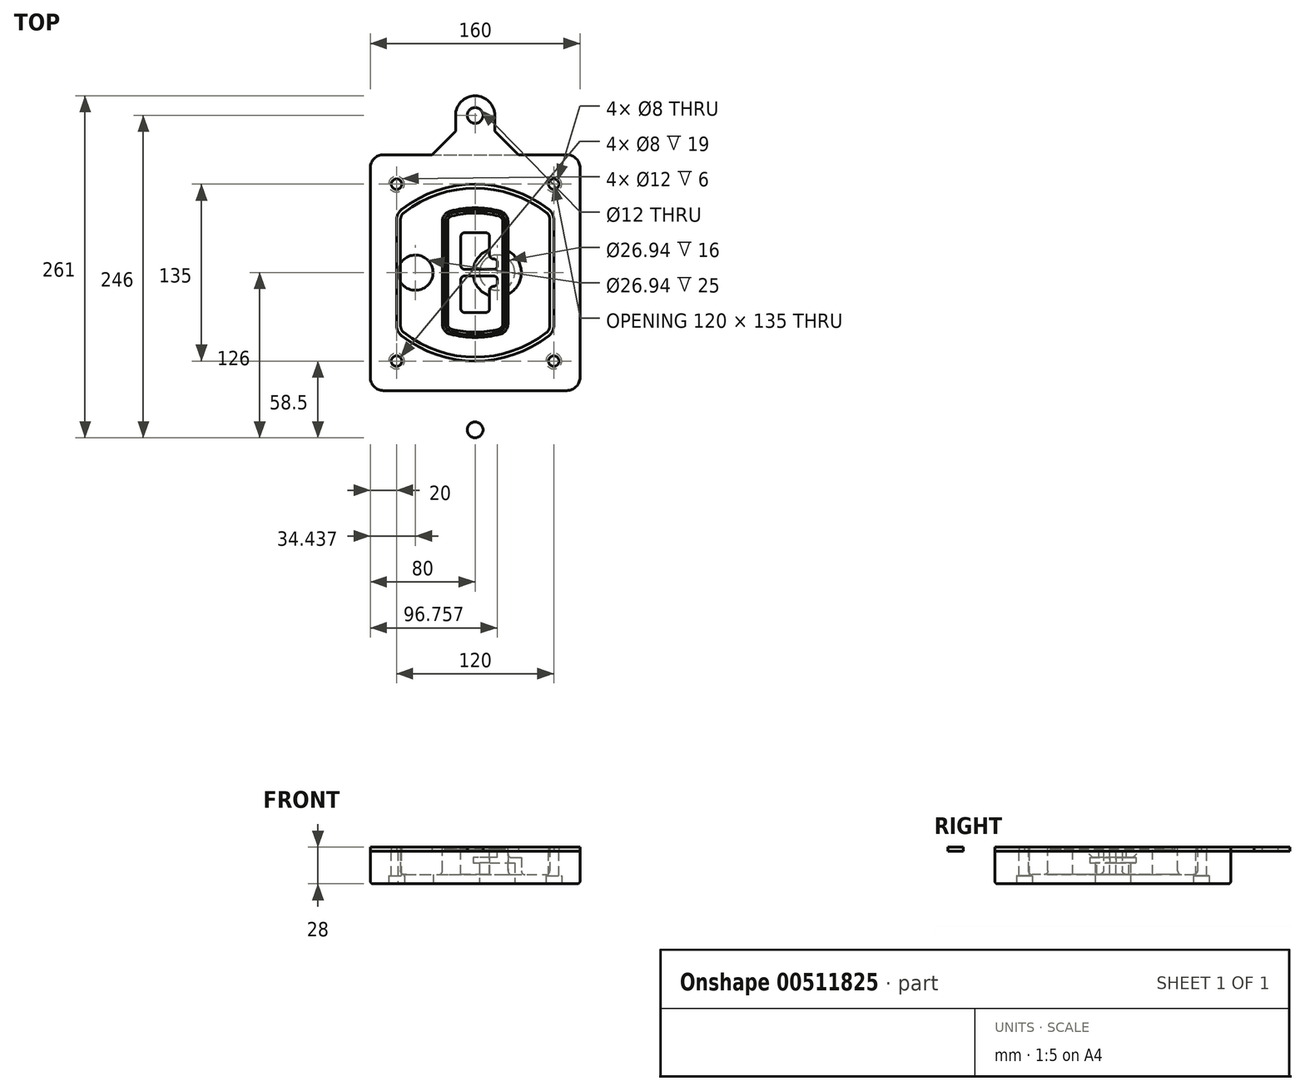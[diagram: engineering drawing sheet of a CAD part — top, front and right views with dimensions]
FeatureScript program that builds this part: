
annotation { "Feature Type Name" : "Feature", "Feature Type Description" : "" }
export const myFeature = defineFeature(function(context is Context, id is Id, definition is map)
    precondition{}
    {
        {
            var Q0;
            Q0=qCreatedBy(makeId("Top.planeOp"),FACE);
            var sketch = newSketch(context, id + "F0", { "sketchPlane" : qUnion([Q0])});
            skPoint(sketch, "E0.rect.middle", {"position": v(0, 0) * mm});
            skLineSegment(sketch, "E1.bottom", {"start": v(-70, -90) * mm, "end": v(70, -90) * mm});
            skLineSegment(sketch, "E1.top", {"start": v(-70, 90) * mm, "end": v(70, 90) * mm});
            skLineSegment(sketch, "E1.left", {"start": v(-80, -80) * mm, "end": v(-80, 80) * mm});
            skLineSegment(sketch, "E1.right", {"start": v(80, -80) * mm, "end": v(80, 80) * mm});
            skLineSegment(sketch, "E2", {"start": v(-80, 90) * mm, "end": v(80, -90) * mm, "construction": true});
            skLineSegment(sketch, "E3", {"start": v(80, 90) * mm, "end": v(-80, -90) * mm, "construction": true});
            skCircle(sketch, "E4", {"center": v(-60, 67.5) * mm, "radius": 4 * mm});
            skCircle(sketch, "E5", {"center": v(60, 67.5) * mm, "radius": 4 * mm});
            skCircle(sketch, "E6", {"center": v(60, -67.5) * mm, "radius": 4 * mm});
            skCircle(sketch, "E7", {"center": v(-60, -67.5) * mm, "radius": 4 * mm});
            skLineSegment(sketch, "E8", {"start": v(-60, 67.5) * mm, "end": v(60, 67.5) * mm, "construction": true});
            skLineSegment(sketch, "E9", {"start": v(60, 67.5) * mm, "end": v(60, -67.5) * mm, "construction": true});
            skLineSegment(sketch, "E10", {"start": v(60, -67.5) * mm, "end": v(-60, -67.5) * mm, "construction": true});
            skLineSegment(sketch, "E11", {"start": v(-60, -67.5) * mm, "end": v(-60, 67.5) * mm, "construction": true});
            skLineSegment(sketch, "E12", {"start": v(-60, 40.3) * mm, "end": v(-60, -40.3) * mm});
            skLineSegment(sketch, "E13", {"start": v(60, 40.3) * mm, "end": v(60, -40.3) * mm});
            skArc(sketch, "E14", {"start": v(56.15, 48.18) * mm, "mid": v(0, 67.5) * mm, "end": v(-56.15, 48.18) * mm});
            skArc(sketch, "E15", {"start": v(-56.15, -48.18) * mm, "mid": v(0, -67.5) * mm, "end": v(56.15, -48.18) * mm});
            skLineSegment(sketch, "E16", {"start": v(-60, 0) * mm, "end": v(60, 0) * mm, "construction": true});
            skPoint(sketch, "E17.visualSharp", {"position": v(-60, -45) * mm});
            skArc(sketch, "E17.filletArc", {"start": v(-60, -40.3) * mm, "mid": v(-58.99, -44.68) * mm, "end": v(-56.15, -48.18) * mm});
            skPoint(sketch, "E18.visualSharp", {"position": v(-60, 45) * mm});
            skArc(sketch, "E18.filletArc", {"start": v(-56.15, 48.18) * mm, "mid": v(-58.99, 44.68) * mm, "end": v(-60, 40.3) * mm});
            skPoint(sketch, "E19.visualSharp", {"position": v(60, 45) * mm});
            skArc(sketch, "E19.filletArc", {"start": v(60, 40.3) * mm, "mid": v(58.99, 44.68) * mm, "end": v(56.15, 48.18) * mm});
            skPoint(sketch, "E20.visualSharp", {"position": v(60, -45) * mm});
            skArc(sketch, "E20.filletArc", {"start": v(56.15, -48.18) * mm, "mid": v(58.99, -44.68) * mm, "end": v(60, -40.3) * mm});
            skPoint(sketch, "E21.visualSharp", {"position": v(-80, 90) * mm});
            skArc(sketch, "E21.filletArc", {"start": v(-70, 90) * mm, "mid": v(-77.07, 87.07) * mm, "end": v(-80, 80) * mm});
            skPoint(sketch, "E22.visualSharp", {"position": v(80, 90) * mm});
            skArc(sketch, "E22.filletArc", {"start": v(80, 80) * mm, "mid": v(77.07, 87.07) * mm, "end": v(70, 90) * mm});
            skPoint(sketch, "E23.visualSharp", {"position": v(80, -90) * mm});
            skArc(sketch, "E23.filletArc", {"start": v(70, -90) * mm, "mid": v(77.07, -87.07) * mm, "end": v(80, -80) * mm});
            skPoint(sketch, "E24.visualSharp", {"position": v(-80, -90) * mm});
            skArc(sketch, "E24.filletArc", {"start": v(-80, -80) * mm, "mid": v(-77.07, -87.07) * mm, "end": v(-70, -90) * mm});
            skArc(sketch, "E25.0", {"start": v(57, 40.3) * mm, "mid": v(56.3, 43.36) * mm, "end": v(54.3, 45.81) * mm});
            skLineSegment(sketch, "E25.1", {"start": v(57, 40.3) * mm, "end": v(57, -40.3) * mm});
            skArc(sketch, "E25.2", {"start": v(54.3, -45.81) * mm, "mid": v(56.3, -43.36) * mm, "end": v(57, -40.3) * mm});
            skArc(sketch, "E25.3", {"start": v(-54.3, -45.81) * mm, "mid": v(0, -64.5) * mm, "end": v(54.3, -45.81) * mm});
            skArc(sketch, "E25.4", {"start": v(-57, -40.3) * mm, "mid": v(-56.3, -43.36) * mm, "end": v(-54.3, -45.81) * mm});
            skArc(sketch, "E25.5", {"start": v(54.3, 45.81) * mm, "mid": v(0, 64.5) * mm, "end": v(-54.3, 45.81) * mm});
            skLineSegment(sketch, "E25.6", {"start": v(-57, 40.3) * mm, "end": v(-57, -40.3) * mm});
            skArc(sketch, "E25.7", {"start": v(-54.3, 45.81) * mm, "mid": v(-56.3, 43.36) * mm, "end": v(-57, 40.3) * mm});
            skArc(sketch, "E26.0", {"start": v(-58.62, 51.33) * mm, "mid": v(-62.58, 46.43) * mm, "end": v(-64, 40.3) * mm});
            skArc(sketch, "E26.1", {"start": v(58.62, 51.33) * mm, "mid": v(0, 71.5) * mm, "end": v(-58.62, 51.33) * mm});
            skArc(sketch, "E26.2", {"start": v(64, 40.3) * mm, "mid": v(62.58, 46.43) * mm, "end": v(58.62, 51.33) * mm});
            skLineSegment(sketch, "E26.3", {"start": v(64, 40.3) * mm, "end": v(64, -40.3) * mm});
            skArc(sketch, "E26.4", {"start": v(58.62, -51.33) * mm, "mid": v(62.58, -46.43) * mm, "end": v(64, -40.3) * mm});
            skLineSegment(sketch, "E26.5", {"start": v(-64, 40.3) * mm, "end": v(-64, -40.3) * mm});
            skArc(sketch, "E26.6", {"start": v(-58.62, -51.33) * mm, "mid": v(0, -71.5) * mm, "end": v(58.62, -51.33) * mm});
            skArc(sketch, "E26.7", {"start": v(-64, -40.3) * mm, "mid": v(-62.58, -46.43) * mm, "end": v(-58.62, -51.33) * mm});
            skSolve(sketch);
        }
        {
            var Q0;
            Q0=makeQuery(id+"F0.imprint","IMPRINT",FACE,{"disambiguationData":[TD([[makeQuery(id+"F0.imprint","IMPRINT",EDGE,{"derivedFrom":sQuery(id+"F0.wireOp",EDGE,"E1.bottom")}),1.0]])]});
            var Q1;
            Q1=makeQuery(id+"F0.imprint","IMPRINT",FACE,{"disambiguationData":[TD([[makeQuery(id+"F0.imprint","IMPRINT",EDGE,{"derivedFrom":sQuery(id+"F0.wireOp",EDGE,"E12")}),1.0]])]});
            var Q2;
            Q2=makeQuery(id+"F0.imprint","IMPRINT",FACE,{"disambiguationData":[TD([[makeQuery(id+"F0.imprint","IMPRINT",EDGE,{"derivedFrom":sQuery(id+"F0.wireOp",EDGE,"E25.0")}),1.0]])]});
            var Q3;
            Q3=makeQuery(id+"F0.imprint","IMPRINT",FACE,{"disambiguationData":[TD([[makeQuery(id+"F0.imprint","IMPRINT",EDGE,{"derivedFrom":sQuery(id+"F0.wireOp",EDGE,"E12")}),-1.0]])]});
            extrude(context, id + "F1", {"entities" : qUnion([Q0, Q1, Q2, Q3]), "oppositeDirection" : true, "depth" : 25 * mm});
        }
        {
            var Q0;
            Q0=makeQuery(id+"F0.imprint","IMPRINT",FACE,{"disambiguationData":[TD([[makeQuery(id+"F0.imprint","IMPRINT",EDGE,{"derivedFrom":sQuery(id+"F0.wireOp",EDGE,"E12")}),1.0]])]});
            extrude(context, id + "F2", {"entities" : qUnion([Q0]), "operationType" : NewBodyOperationType.ADD, "depth" : 3 * mm});
        }
        {
            var Q0;
            Q0=makeQuery(id+"F0.imprint","IMPRINT",FACE,{"disambiguationData":[TD([[makeQuery(id+"F0.imprint","IMPRINT",EDGE,{"derivedFrom":sQuery(id+"F0.wireOp",EDGE,"E25.0")}),1.0]])]});
            extrude(context, id + "F3", {"entities" : qUnion([Q0]), "operationType" : NewBodyOperationType.REMOVE, "oppositeDirection" : true, "depth" : 18 * mm});
        }
        {
            var Q0;
            Q0=makeQuery(id+"F2.opExtrude","CAP_FACE",FACE,{"disambiguationData":[OSD([sQuery(id+"F0.wireOp",EDGE,"E12"),sQuery(id+"F0.wireOp",EDGE,"E13"),sQuery(id+"F0.wireOp",EDGE,"E14"),sQuery(id+"F0.wireOp",EDGE,"E15"),sQuery(id+"F0.wireOp",EDGE,"E17.filletArc"),sQuery(id+"F0.wireOp",EDGE,"E18.filletArc"),sQuery(id+"F0.wireOp",EDGE,"E19.filletArc"),sQuery(id+"F0.wireOp",EDGE,"E20.filletArc"),sQuery(id+"F0.wireOp",EDGE,"E25.0"),sQuery(id+"F0.wireOp",EDGE,"E25.1"),sQuery(id+"F0.wireOp",EDGE,"E25.2"),sQuery(id+"F0.wireOp",EDGE,"E25.3"),sQuery(id+"F0.wireOp",EDGE,"E25.4"),sQuery(id+"F0.wireOp",EDGE,"E25.5"),sQuery(id+"F0.wireOp",EDGE,"E25.6"),sQuery(id+"F0.wireOp",EDGE,"E25.7")])],"isStart":false});
            var sketch = newSketch(context, id + "F4", { "sketchPlane" : qUnion([Q0])});
            skArc(sketch, "E27.0", {"start": v(-19.08, -46.97) * mm, "mid": v(0, -49.5) * mm, "end": v(19.08, -46.97) * mm});
            skArc(sketch, "E28.0", {"start": v(19.08, 46.97) * mm, "mid": v(0, 49.5) * mm, "end": v(-19.08, 46.97) * mm});
            skLineSegment(sketch, "E29", {"start": v(-25, 39.25) * mm, "end": v(-25, -39.25) * mm});
            skLineSegment(sketch, "E30", {"start": v(25, 39.25) * mm, "end": v(25, -39.25) * mm});
            skLineSegment(sketch, "E31", {"start": v(-25, 45.1) * mm, "end": v(25, 45.1) * mm, "construction": true});
            skLineSegment(sketch, "E32", {"start": v(-25, -45.1) * mm, "end": v(25, -45.1) * mm, "construction": true});
            skPoint(sketch, "E33.visualSharp", {"position": v(-25, 45.1) * mm});
            skArc(sketch, "E33.filletArc", {"start": v(-19.08, 46.97) * mm, "mid": v(-23.35, 44.11) * mm, "end": v(-25, 39.25) * mm});
            skPoint(sketch, "E34.visualSharp", {"position": v(25, 45.1) * mm});
            skArc(sketch, "E34.filletArc", {"start": v(25, 39.25) * mm, "mid": v(23.35, 44.11) * mm, "end": v(19.08, 46.97) * mm});
            skPoint(sketch, "E35.visualSharp", {"position": v(25, -45.1) * mm});
            skArc(sketch, "E35.filletArc", {"start": v(19.08, -46.97) * mm, "mid": v(23.35, -44.11) * mm, "end": v(25, -39.25) * mm});
            skPoint(sketch, "E36.visualSharp", {"position": v(-25, -45.1) * mm});
            skArc(sketch, "E36.filletArc", {"start": v(-25, -39.25) * mm, "mid": v(-23.35, -44.11) * mm, "end": v(-19.08, -46.97) * mm});
            skArc(sketch, "E37.0", {"start": v(54.3, 45.81) * mm, "mid": v(0, 64.5) * mm, "end": v(-54.3, 45.81) * mm});
            skArc(sketch, "E37.1", {"start": v(-54.3, 45.81) * mm, "mid": v(-56.3, 43.36) * mm, "end": v(-57, 40.3) * mm});
            skLineSegment(sketch, "E37.2", {"start": v(-57, 40.3) * mm, "end": v(-57, -40.3) * mm});
            skArc(sketch, "E37.3", {"start": v(-57, -40.3) * mm, "mid": v(-56.3, -43.36) * mm, "end": v(-54.3, -45.81) * mm});
            skArc(sketch, "E37.4", {"start": v(-54.3, -45.81) * mm, "mid": v(0, -64.5) * mm, "end": v(54.3, -45.81) * mm});
            skArc(sketch, "E37.5", {"start": v(54.3, -45.81) * mm, "mid": v(56.3, -43.36) * mm, "end": v(57, -40.3) * mm});
            skLineSegment(sketch, "E37.6", {"start": v(57, 40.3) * mm, "end": v(57, -40.3) * mm});
            skArc(sketch, "E37.7", {"start": v(57, 40.3) * mm, "mid": v(56.3, 43.36) * mm, "end": v(54.3, 45.81) * mm});
            skLineSegment(sketch, "E38.0", {"start": v(23, 39.25) * mm, "end": v(23, -39.25) * mm});
            skArc(sketch, "E38.1", {"start": v(18.56, -45.04) * mm, "mid": v(21.76, -42.9) * mm, "end": v(23, -39.25) * mm});
            skArc(sketch, "E38.2", {"start": v(-18.56, -45.04) * mm, "mid": v(0, -47.5) * mm, "end": v(18.56, -45.04) * mm});
            skArc(sketch, "E38.3", {"start": v(-23, -39.25) * mm, "mid": v(-21.76, -42.9) * mm, "end": v(-18.56, -45.04) * mm});
            skLineSegment(sketch, "E38.4", {"start": v(-23, 39.25) * mm, "end": v(-23, -39.25) * mm});
            skArc(sketch, "E38.5", {"start": v(23, 39.25) * mm, "mid": v(21.76, 42.9) * mm, "end": v(18.56, 45.04) * mm});
            skArc(sketch, "E38.6", {"start": v(-18.56, 45.04) * mm, "mid": v(-21.76, 42.9) * mm, "end": v(-23, 39.25) * mm});
            skArc(sketch, "E38.7", {"start": v(18.56, 45.04) * mm, "mid": v(0, 47.5) * mm, "end": v(-18.56, 45.04) * mm});
            skArc(sketch, "E39.0", {"start": v(21, 39.25) * mm, "mid": v(20.18, 41.68) * mm, "end": v(18.04, 43.1) * mm});
            skLineSegment(sketch, "E39.1", {"start": v(21, 39.25) * mm, "end": v(21, -39.25) * mm});
            skArc(sketch, "E39.2", {"start": v(18.04, -43.1) * mm, "mid": v(20.18, -41.68) * mm, "end": v(21, -39.25) * mm});
            skArc(sketch, "E39.3", {"start": v(-18.04, -43.1) * mm, "mid": v(0, -45.5) * mm, "end": v(18.04, -43.1) * mm});
            skArc(sketch, "E39.4", {"start": v(-21, -39.25) * mm, "mid": v(-20.18, -41.68) * mm, "end": v(-18.04, -43.1) * mm});
            skArc(sketch, "E39.5", {"start": v(18.04, 43.1) * mm, "mid": v(0, 45.5) * mm, "end": v(-18.04, 43.1) * mm});
            skLineSegment(sketch, "E39.6", {"start": v(-21, 39.25) * mm, "end": v(-21, -39.25) * mm});
            skArc(sketch, "E39.7", {"start": v(-18.04, 43.1) * mm, "mid": v(-20.18, 41.68) * mm, "end": v(-21, 39.25) * mm});
            skLineSegment(sketch, "E40", {"start": v(-25, 0) * mm, "end": v(25, 0) * mm, "construction": true});
            skLineSegment(sketch, "E41", {"start": v(-11, 5.5) * mm, "end": v(-11, 27.5) * mm});
            skLineSegment(sketch, "E42", {"start": v(-8, 30.5) * mm, "end": v(8, 30.5) * mm});
            skLineSegment(sketch, "E43", {"start": v(11, 27.5) * mm, "end": v(11, 13.5) * mm});
            skLineSegment(sketch, "E44", {"start": v(14, 10.5) * mm, "end": v(14, 10.5) * mm});
            skLineSegment(sketch, "E45", {"start": v(17, 7.5) * mm, "end": v(17, 5.5) * mm});
            skLineSegment(sketch, "E46", {"start": v(14, 2.5) * mm, "end": v(-8, 2.5) * mm});
            skPoint(sketch, "E47.visualSharp", {"position": v(-11, 30.5) * mm});
            skArc(sketch, "E47.filletArc", {"start": v(-8, 30.5) * mm, "mid": v(-10.12, 29.62) * mm, "end": v(-11, 27.5) * mm});
            skPoint(sketch, "E48.visualSharp", {"position": v(11, 30.5) * mm});
            skArc(sketch, "E48.filletArc", {"start": v(11, 27.5) * mm, "mid": v(10.12, 29.62) * mm, "end": v(8, 30.5) * mm});
            skPoint(sketch, "E49.visualSharp", {"position": v(11, 10.5) * mm});
            skArc(sketch, "E49.filletArc", {"start": v(11, 13.5) * mm, "mid": v(11.88, 11.38) * mm, "end": v(14, 10.5) * mm});
            skPoint(sketch, "E50.visualSharp", {"position": v(17, 10.5) * mm});
            skArc(sketch, "E50.filletArc", {"start": v(17, 7.5) * mm, "mid": v(16.12, 9.62) * mm, "end": v(14, 10.5) * mm});
            skPoint(sketch, "E51.visualSharp", {"position": v(17, 2.5) * mm});
            skArc(sketch, "E51.filletArc", {"start": v(14, 2.5) * mm, "mid": v(16.12, 3.38) * mm, "end": v(17, 5.5) * mm});
            skPoint(sketch, "E52.visualSharp", {"position": v(-11, 2.5) * mm});
            skArc(sketch, "E52.filletArc", {"start": v(-11, 5.5) * mm, "mid": v(-10.12, 3.38) * mm, "end": v(-8, 2.5) * mm});
            skLineSegment(sketch, "E53.0.MirrorCS", {"start": v(14, -2.5) * mm, "end": v(-8, -2.5) * mm});
            skArc(sketch, "E54.0.MirrorCS", {"start": v(-11, -5.5) * mm, "mid": v(-10.12, -3.38) * mm, "end": v(-8, -2.5) * mm});
            skLineSegment(sketch, "E55.0.MirrorCS", {"start": v(-11, -5.5) * mm, "end": v(-11, -27.5) * mm});
            skArc(sketch, "E56.0.MirrorCS", {"start": v(-8, -30.5) * mm, "mid": v(-10.12, -29.62) * mm, "end": v(-11, -27.5) * mm});
            skLineSegment(sketch, "E57.0.MirrorCS", {"start": v(-8, -30.5) * mm, "end": v(8, -30.5) * mm});
            skArc(sketch, "E58.0.MirrorCS", {"start": v(11, -27.5) * mm, "mid": v(10.12, -29.62) * mm, "end": v(8, -30.5) * mm});
            skLineSegment(sketch, "E59.0.MirrorCS", {"start": v(11, -27.5) * mm, "end": v(11, -13.5) * mm});
            skArc(sketch, "E60.0.MirrorCS", {"start": v(11, -13.5) * mm, "mid": v(11.88, -11.38) * mm, "end": v(14, -10.5) * mm});
            skArc(sketch, "E61.0.MirrorCS", {"start": v(17, -7.5) * mm, "mid": v(16.12, -9.62) * mm, "end": v(14, -10.5) * mm});
            skLineSegment(sketch, "E62.0.MirrorCS", {"start": v(17, -7.5) * mm, "end": v(17, -5.5) * mm});
            skArc(sketch, "E63.0.MirrorCS", {"start": v(14, -2.5) * mm, "mid": v(16.12, -3.38) * mm, "end": v(17, -5.5) * mm});
            skSolve(sketch);
        }
        {
            var Q0;
            Q0=makeQuery(id+"F4.imprint","IMPRINT",FACE,{"disambiguationData":[TD([[makeQuery(id+"F4.imprint","IMPRINT",EDGE,{"derivedFrom":sQuery(id+"F4.wireOp",EDGE,"E27.0")}),1.0]])]});
            var Q1;
            Q1=makeQuery(id+"F4.imprint","IMPRINT",FACE,{"disambiguationData":[TD([[makeQuery(id+"F4.imprint","IMPRINT",EDGE,{"derivedFrom":sQuery(id+"F4.wireOp",EDGE,"E38.0")}),-1.0]])]});
            var Q2;
            Q2=makeQuery(id+"F4.imprint","IMPRINT",FACE,{"disambiguationData":[TD([[makeQuery(id+"F4.imprint","IMPRINT",EDGE,{"derivedFrom":sQuery(id+"F4.wireOp",EDGE,"E39.0")}),1.0]])]});
            extrude(context, id + "F5", {"entities" : qUnion([Q0, Q1, Q2]), "operationType" : NewBodyOperationType.ADD, "endBound" : BoundingType.UP_TO_NEXT, "oppositeDirection" : true, "depth" : 25 * mm});
        }
        {
            var Q0;
            Q0=makeQuery(id+"F4.imprint","IMPRINT",FACE,{"disambiguationData":[TD([[makeQuery(id+"F4.imprint","IMPRINT",EDGE,{"derivedFrom":sQuery(id+"F4.wireOp",EDGE,"E38.0")}),-1.0]])]});
            extrude(context, id + "F6", {"entities" : qUnion([Q0]), "operationType" : NewBodyOperationType.REMOVE, "oppositeDirection" : true, "depth" : 2 * mm});
        }
        {
            var Q0;
            Q0=makeQuery(id+"F1.opExtrude","CAP_FACE",FACE,{"disambiguationData":[OSD([sQuery(id+"F0.wireOp",EDGE,"E1.bottom"),sQuery(id+"F0.wireOp",EDGE,"E1.top"),sQuery(id+"F0.wireOp",EDGE,"E1.left"),sQuery(id+"F0.wireOp",EDGE,"E1.right"),sQuery(id+"F0.wireOp",EDGE,"E4"),sQuery(id+"F0.wireOp",EDGE,"E5"),sQuery(id+"F0.wireOp",EDGE,"E6"),sQuery(id+"F0.wireOp",EDGE,"E7"),sQuery(id+"F0.wireOp",EDGE,"E21.filletArc"),sQuery(id+"F0.wireOp",EDGE,"E22.filletArc"),sQuery(id+"F0.wireOp",EDGE,"E23.filletArc"),sQuery(id+"F0.wireOp",EDGE,"E24.filletArc")])],"isStart":false});
            var sketch = newSketch(context, id + "F7", { "sketchPlane" : qUnion([Q0])});
            skCircle(sketch, "E64", {"center": v(16.76, 0) * mm, "radius": 13.47 * mm});
            skCircle(sketch, "E65", {"center": v(-45.56, 0) * mm, "radius": 13.47 * mm});
            skLineSegment(sketch, "E66", {"start": v(80, 0) * mm, "end": v(-80, 0) * mm});
            skCircle(sketch, "E67", {"center": v(16.76, 0) * mm, "radius": 18.47 * mm});
            skCircle(sketch, "E68", {"center": v(60, -67.5) * mm, "radius": 6 * mm});
            skCircle(sketch, "E69", {"center": v(-60, -67.5) * mm, "radius": 6 * mm});
            skCircle(sketch, "E70", {"center": v(-60, 67.5) * mm, "radius": 6 * mm});
            skCircle(sketch, "E71", {"center": v(60, 67.5) * mm, "radius": 6 * mm});
            skSolve(sketch);
        }
        {
            var Q0;
            {var subQ1=sQuery(id+"F7.wireOp",EDGE,"E66");var subQ4=sQuery(id+"F7.wireOp",EDGE,"E64");var subQ6=makeQuery(id+"F7.imprint","INTERSECT",VERTEX,{"disambiguationData":[OD(0.0)],"derivedFrom":[subQ4,subQ1]});Q0=makeQuery(id+"F7.imprint","IMPRINT",FACE,{"disambiguationData":[TD([[makeQuery(id+"F7.imprint","IMPRINT",EDGE,{"disambiguationData":[TD([[subQ6,-1.0]])],"derivedFrom":subQ4}),-1.0]])]});}
            var Q1;
            {var subQ0=sQuery(id+"F7.wireOp",EDGE,"E66");var subQ1=sQuery(id+"F7.wireOp",EDGE,"E64");var subQ3=makeQuery(id+"F7.imprint","INTERSECT",VERTEX,{"disambiguationData":[OD(0.0)],"derivedFrom":[subQ1,subQ0]});Q1=makeQuery(id+"F7.imprint","IMPRINT",FACE,{"disambiguationData":[TD([[makeQuery(id+"F7.imprint","IMPRINT",EDGE,{"disambiguationData":[TD([[subQ3,-1.0]])],"derivedFrom":subQ1}),1.0]])]});}
            var Q2;
            {var subQ0=sQuery(id+"F7.wireOp",EDGE,"E66");var subQ1=sQuery(id+"F7.wireOp",EDGE,"E64");var subQ3=makeQuery(id+"F7.imprint","INTERSECT",VERTEX,{"disambiguationData":[OD(0.0)],"derivedFrom":[subQ1,subQ0]});Q2=makeQuery(id+"F7.imprint","IMPRINT",FACE,{"disambiguationData":[TD([[makeQuery(id+"F7.imprint","IMPRINT",EDGE,{"disambiguationData":[TD([[subQ3,1.0]])],"derivedFrom":subQ1}),1.0]])]});}
            var Q3;
            {var subQ1=sQuery(id+"F7.wireOp",EDGE,"E66");var subQ4=sQuery(id+"F7.wireOp",EDGE,"E64");var subQ6=makeQuery(id+"F7.imprint","INTERSECT",VERTEX,{"disambiguationData":[OD(0.0)],"derivedFrom":[subQ4,subQ1]});Q3=makeQuery(id+"F7.imprint","IMPRINT",FACE,{"disambiguationData":[TD([[makeQuery(id+"F7.imprint","IMPRINT",EDGE,{"disambiguationData":[TD([[subQ6,1.0]])],"derivedFrom":subQ4}),-1.0]])]});}
            extrude(context, id + "F8", {"entities" : qUnion([Q0, Q1, Q2, Q3]), "operationType" : NewBodyOperationType.ADD, "oppositeDirection" : true, "depth" : 20 * mm});
        }
        {
            var Q0;
            {var subQ0=sQuery(id+"F7.wireOp",EDGE,"E66");var subQ1=sQuery(id+"F7.wireOp",EDGE,"E64");var subQ3=makeQuery(id+"F7.imprint","INTERSECT",VERTEX,{"disambiguationData":[OD(0.0)],"derivedFrom":[subQ1,subQ0]});Q0=makeQuery(id+"F7.imprint","IMPRINT",FACE,{"disambiguationData":[TD([[makeQuery(id+"F7.imprint","IMPRINT",EDGE,{"disambiguationData":[TD([[subQ3,-1.0]])],"derivedFrom":subQ1}),1.0]])]});}
            var Q1;
            {var subQ0=sQuery(id+"F7.wireOp",EDGE,"E66");var subQ1=sQuery(id+"F7.wireOp",EDGE,"E64");var subQ3=makeQuery(id+"F7.imprint","INTERSECT",VERTEX,{"disambiguationData":[OD(0.0)],"derivedFrom":[subQ1,subQ0]});Q1=makeQuery(id+"F7.imprint","IMPRINT",FACE,{"disambiguationData":[TD([[makeQuery(id+"F7.imprint","IMPRINT",EDGE,{"disambiguationData":[TD([[subQ3,1.0]])],"derivedFrom":subQ1}),1.0]])]});}
            extrude(context, id + "F9", {"entities" : qUnion([Q0, Q1]), "operationType" : NewBodyOperationType.REMOVE, "oppositeDirection" : true, "depth" : 16 * mm});
        }
        {
            var Q0;
            {var subQ0=sQuery(id+"F7.wireOp",EDGE,"E66");var subQ1=sQuery(id+"F7.wireOp",EDGE,"E65");var subQ3=makeQuery(id+"F7.imprint","INTERSECT",VERTEX,{"disambiguationData":[OD(0.0)],"derivedFrom":[subQ1,subQ0]});Q0=makeQuery(id+"F7.imprint","IMPRINT",FACE,{"disambiguationData":[TD([[makeQuery(id+"F7.imprint","IMPRINT",EDGE,{"disambiguationData":[TD([[subQ3,-1.0]])],"derivedFrom":subQ1}),1.0]])]});}
            var Q1;
            {var subQ0=sQuery(id+"F7.wireOp",EDGE,"E66");var subQ1=sQuery(id+"F7.wireOp",EDGE,"E65");var subQ3=makeQuery(id+"F7.imprint","INTERSECT",VERTEX,{"disambiguationData":[OD(0.0)],"derivedFrom":[subQ1,subQ0]});Q1=makeQuery(id+"F7.imprint","IMPRINT",FACE,{"disambiguationData":[TD([[makeQuery(id+"F7.imprint","IMPRINT",EDGE,{"disambiguationData":[TD([[subQ3,1.0]])],"derivedFrom":subQ1}),1.0]])]});}
            extrude(context, id + "F10", {"entities" : qUnion([Q0, Q1]), "operationType" : NewBodyOperationType.REMOVE, "oppositeDirection" : true, "depth" : 25 * mm});
        }
        {
            var Q0;
            Q0=makeQuery(id+"F7.imprint","IMPRINT",FACE,{"disambiguationData":[TD([[makeQuery(id+"F7.imprint","IMPRINT",EDGE,{"derivedFrom":sQuery(id+"F7.wireOp",EDGE,"E68")}),1.0]])]});
            var Q1;
            Q1=makeQuery(id+"F7.imprint","IMPRINT",FACE,{"disambiguationData":[TD([[makeQuery(id+"F7.imprint","IMPRINT",EDGE,{"derivedFrom":makeQuery(id+"F1.opExtrude","CAP_EDGE",EDGE,{"disambiguationData":[OSD([sQuery(id+"F0.wireOp",EDGE,"E5")])],"isStart":false})}),-1.0]])]});
            var Q2;
            Q2=makeQuery(id+"F7.imprint","IMPRINT",FACE,{"disambiguationData":[TD([[makeQuery(id+"F7.imprint","IMPRINT",EDGE,{"derivedFrom":sQuery(id+"F7.wireOp",EDGE,"E69")}),1.0]])]});
            var Q3;
            Q3=makeQuery(id+"F7.imprint","IMPRINT",FACE,{"disambiguationData":[TD([[makeQuery(id+"F7.imprint","IMPRINT",EDGE,{"derivedFrom":makeQuery(id+"F1.opExtrude","CAP_EDGE",EDGE,{"disambiguationData":[OSD([sQuery(id+"F0.wireOp",EDGE,"E4")])],"isStart":false})}),-1.0]])]});
            var Q4;
            Q4=makeQuery(id+"F7.imprint","IMPRINT",FACE,{"disambiguationData":[TD([[makeQuery(id+"F7.imprint","IMPRINT",EDGE,{"derivedFrom":sQuery(id+"F7.wireOp",EDGE,"E70")}),1.0]])]});
            var Q5;
            Q5=makeQuery(id+"F7.imprint","IMPRINT",FACE,{"disambiguationData":[TD([[makeQuery(id+"F7.imprint","IMPRINT",EDGE,{"derivedFrom":makeQuery(id+"F1.opExtrude","CAP_EDGE",EDGE,{"disambiguationData":[OSD([sQuery(id+"F0.wireOp",EDGE,"E7")])],"isStart":false})}),-1.0]])]});
            var Q6;
            Q6=makeQuery(id+"F7.imprint","IMPRINT",FACE,{"disambiguationData":[TD([[makeQuery(id+"F7.imprint","IMPRINT",EDGE,{"derivedFrom":sQuery(id+"F7.wireOp",EDGE,"E71")}),1.0]])]});
            var Q7;
            Q7=makeQuery(id+"F7.imprint","IMPRINT",FACE,{"disambiguationData":[TD([[makeQuery(id+"F7.imprint","IMPRINT",EDGE,{"derivedFrom":makeQuery(id+"F1.opExtrude","CAP_EDGE",EDGE,{"disambiguationData":[OSD([sQuery(id+"F0.wireOp",EDGE,"E6")])],"isStart":false})}),-1.0]])]});
            extrude(context, id + "F11", {"entities" : qUnion([Q0, Q1, Q2, Q3, Q4, Q5, Q6, Q7]), "operationType" : NewBodyOperationType.REMOVE, "oppositeDirection" : true, "depth" : 6 * mm});
        }
        {
            var Q0;
            Q0=makeQuery(id+"F9.boolean.opBoolean","COPY",FACE,{"derivedFrom":makeQuery(id+"F9.opExtrude","CAP_FACE",FACE,{"disambiguationData":[OSD([sQuery(id+"F7.wireOp",EDGE,"E64")])],"isStart":false})});
            var sketch = newSketch(context, id + "F12", { "sketchPlane" : qUnion([Q0])});
            skArc(sketch, "E72.0", {"start": v(11, 17.55) * mm, "mid": v(2.57, 11.82) * mm, "end": v(-1.54, 2.5) * mm});
            skArc(sketch, "E72.1", {"start": v(-1.54, -2.5) * mm, "mid": v(2.57, -11.82) * mm, "end": v(11, -17.55) * mm});
            skLineSegment(sketch, "E73", {"start": v(-1.54, -2.5) * mm, "end": v(14, -2.5) * mm});
            skLineSegment(sketch, "E74.0", {"start": v(14, 2.5) * mm, "end": v(-1.54, 2.5) * mm});
            skArc(sketch, "E74.1", {"start": v(14, 2.5) * mm, "mid": v(16.12, 3.38) * mm, "end": v(17, 5.5) * mm});
            skLineSegment(sketch, "E74.2", {"start": v(17, 7.5) * mm, "end": v(17, 5.5) * mm});
            skArc(sketch, "E74.3", {"start": v(17, 7.5) * mm, "mid": v(16.12, 9.62) * mm, "end": v(14, 10.5) * mm});
            skArc(sketch, "E74.4", {"start": v(11, 13.5) * mm, "mid": v(11.88, 11.38) * mm, "end": v(14, 10.5) * mm});
            skLineSegment(sketch, "E74.5", {"start": v(11, 17.55) * mm, "end": v(11, 13.5) * mm});
            skLineSegment(sketch, "E74.7", {"start": v(14, -2.5) * mm, "end": v(-1.54, -2.5) * mm});
            skArc(sketch, "E74.8", {"start": v(14, -2.5) * mm, "mid": v(16.12, -3.38) * mm, "end": v(17, -5.5) * mm});
            skLineSegment(sketch, "E74.9", {"start": v(17, -7.5) * mm, "end": v(17, -5.5) * mm});
            skArc(sketch, "E74.10", {"start": v(17, -7.5) * mm, "mid": v(16.12, -9.62) * mm, "end": v(14, -10.5) * mm});
            skArc(sketch, "E74.11", {"start": v(11, -13.5) * mm, "mid": v(11.88, -11.38) * mm, "end": v(14, -10.5) * mm});
            skLineSegment(sketch, "E74.12", {"start": v(11, -17.55) * mm, "end": v(11, -13.5) * mm});
            skPoint(sketch, "E75.orphan", {"position": v(11, -27.5) * mm});
            skPoint(sketch, "E76.orphan", {"position": v(-8, -2.5) * mm});
            skPoint(sketch, "E77.orphan", {"position": v(-8, 2.5) * mm});
            skPoint(sketch, "E78.orphan", {"position": v(11, 27.5) * mm});
            skSolve(sketch);
        }
        {
            var Q0;
            {var subQ7=sQuery(id+"F12.wireOp",EDGE,"E72.0");var subQ14=sQuery(id+"F12.wireOp",EDGE,"E72.1");var subQ16=sQuery(id+"F12.wireOp",EDGE,"E74.1");var subQ18=sQuery(id+"F12.wireOp",EDGE,"E74.8");Q0=qUnion([makeQuery(id+"F12.imprint","IMPRINT",FACE,{"disambiguationData":[TD([[makeQuery(id+"F12.imprint","IMPRINT",EDGE,{"derivedFrom":subQ7}),1.0]])]}),makeQuery(id+"F12.imprint","IMPRINT",FACE,{"disambiguationData":[TD([[makeQuery(id+"F12.imprint","IMPRINT",EDGE,{"derivedFrom":subQ14}),1.0]])]}),makeQuery(id+"F12.imprint","IMPRINT",FACE,{"disambiguationData":[TD([[makeQuery(id+"F12.imprint","IMPRINT",EDGE,{"derivedFrom":subQ16}),1.0]])]}),makeQuery(id+"F12.imprint","IMPRINT",FACE,{"disambiguationData":[TD([[makeQuery(id+"F12.imprint","IMPRINT",EDGE,{"derivedFrom":subQ18}),-1.0]])]})]);}
            var Q1;
            Q1=makeQuery(id+"F5.boolean.opBoolean","SPLIT",FACE,{"disambiguationData":[TD([makeQuery(id+"F5.opExtrude","SWEPT_FACE",FACE,{"disambiguationData":[OSD([sQuery(id+"F4.wireOp",EDGE,"E41")])]})])],"derivedFrom":makeQuery(id+"F3.boolean.opBoolean","COPY",FACE,{"derivedFrom":makeQuery(id+"F3.opExtrude","CAP_FACE",FACE,{"disambiguationData":[OSD([sQuery(id+"F0.wireOp",EDGE,"E25.0"),sQuery(id+"F0.wireOp",EDGE,"E25.1"),sQuery(id+"F0.wireOp",EDGE,"E25.2"),sQuery(id+"F0.wireOp",EDGE,"E25.3"),sQuery(id+"F0.wireOp",EDGE,"E25.4"),sQuery(id+"F0.wireOp",EDGE,"E25.5"),sQuery(id+"F0.wireOp",EDGE,"E25.6"),sQuery(id+"F0.wireOp",EDGE,"E25.7")])],"isStart":false})})});
            extrude(context, id + "F13", {"entities" : qUnion([Q0]), "operationType" : NewBodyOperationType.REMOVE, "endBound" : BoundingType.UP_TO_SURFACE, "endBoundEntityFace" : qUnion([Q1]), "depth" : 25 * mm});
        }
        {
            var Q0;
            Q0=makeQuery(id+"F3.boolean.opBoolean","COPY",EDGE,{"derivedFrom":makeQuery(id+"F3.opExtrude","CAP_EDGE",EDGE,{"disambiguationData":[OSD([sQuery(id+"F0.wireOp",EDGE,"E25.6")])],"isStart":false})});
            var Q1;
            Q1=makeQuery(id+"F8.boolean.opBoolean","INTERSECT",EDGE,{"derivedFrom":[makeQuery(id+"F5.opExtrude","SWEPT_FACE",FACE,{"disambiguationData":[OSD([sQuery(id+"F4.wireOp",EDGE,"E30")])]}),makeQuery(id+"F8.opExtrude","CAP_FACE",FACE,{"disambiguationData":[OSD([sQuery(id+"F7.wireOp",EDGE,"E67")])],"isStart":false})]});
            var Q2;
            Q2=makeQuery(id+"F8.boolean.opBoolean","INTERSECT",EDGE,{"disambiguationData":[OD(1.0)],"derivedFrom":[makeQuery(id+"F5.opExtrude","SWEPT_FACE",FACE,{"disambiguationData":[OSD([sQuery(id+"F4.wireOp",EDGE,"E30")])]}),makeQuery(id+"F8.opExtrude","SWEPT_FACE",FACE,{"disambiguationData":[OSD([sQuery(id+"F7.wireOp",EDGE,"E67")])]})]});
            var Q3;
            {var subQ0=sQuery(id+"F4.wireOp",EDGE,"E30");Q3=makeQuery(id+"F8.boolean.opBoolean","SPLIT",EDGE,{"disambiguationData":[TD([makeQuery(id+"F5.opExtrude","SWEPT_FACE",FACE,{"disambiguationData":[OSD([sQuery(id+"F4.wireOp",EDGE,"E35.filletArc")])]})])],"derivedFrom":makeQuery(id+"F5.opExtrude","CAP_EDGE",EDGE,{"disambiguationData":[OSD([subQ0])],"isStart":false})});}
            var Q4;
            {var subQ0=sQuery(id+"F0.wireOp",EDGE,"E25.7");var subQ1=sQuery(id+"F0.wireOp",EDGE,"E25.1");var subQ2=sQuery(id+"F0.wireOp",EDGE,"E25.6");var subQ3=sQuery(id+"F0.wireOp",EDGE,"E25.5");var subQ4=sQuery(id+"F0.wireOp",EDGE,"E25.4");var subQ5=sQuery(id+"F0.wireOp",EDGE,"E25.0");var subQ6=sQuery(id+"F0.wireOp",EDGE,"E25.2");var subQ7=sQuery(id+"F0.wireOp",EDGE,"E25.3");Q4=makeQuery(id+"F8.boolean.opBoolean","INTERSECT",EDGE,{"derivedFrom":[makeQuery(id+"F5.boolean.opBoolean","SPLIT",FACE,{"disambiguationData":[TD([makeQuery(id+"F2.opExtrude","SWEPT_FACE",FACE,{"disambiguationData":[OSD([subQ5])]})])],"derivedFrom":makeQuery(id+"F3.boolean.opBoolean","COPY",FACE,{"derivedFrom":makeQuery(id+"F3.opExtrude","CAP_FACE",FACE,{"disambiguationData":[OSD([subQ5,subQ1,subQ6,subQ7,subQ4,subQ3,subQ2,subQ0])],"isStart":false})})}),makeQuery(id+"F8.opExtrude","SWEPT_FACE",FACE,{"disambiguationData":[OSD([sQuery(id+"F7.wireOp",EDGE,"E67")])]})]});}
            var Q5;
            Q5=makeQuery(id+"F8.boolean.opBoolean","INTERSECT",EDGE,{"disambiguationData":[OD(0.0)],"derivedFrom":[makeQuery(id+"F5.opExtrude","SWEPT_FACE",FACE,{"disambiguationData":[OSD([sQuery(id+"F4.wireOp",EDGE,"E30")])]}),makeQuery(id+"F8.opExtrude","SWEPT_FACE",FACE,{"disambiguationData":[OSD([sQuery(id+"F7.wireOp",EDGE,"E67")])]})]});
            fillet(context, id + "F14", {"entities" : qUnion([Q0, Q1, Q2, Q3, Q4, Q5]), "radius" : 3 * mm, "tangentPropagation" : true, "allowEdgeOverflow" : false});
        }
        {
            var Q0;
            Q0=makeQuery(id+"F1.opExtrude","CAP_EDGE",EDGE,{"disambiguationData":[OSD([sQuery(id+"F0.wireOp",EDGE,"E1.bottom")])],"isStart":false});
            fillet(context, id + "F15", {"entities" : qUnion([Q0]), "radius" : 2 * mm, "tangentPropagation" : true, "allowEdgeOverflow" : false});
        }
        {
            var Q0;
            {var subQ0=sQuery(id+"F0.wireOp",EDGE,"E21.filletArc");var subQ1=sQuery(id+"F0.wireOp",EDGE,"E7");var subQ2=sQuery(id+"F0.wireOp",EDGE,"E6");var subQ3=sQuery(id+"F0.wireOp",EDGE,"E5");var subQ4=sQuery(id+"F0.wireOp",EDGE,"E4");var subQ5=sQuery(id+"F0.wireOp",EDGE,"E22.filletArc");var subQ6=sQuery(id+"F0.wireOp",EDGE,"E1.bottom");var subQ7=sQuery(id+"F0.wireOp",EDGE,"E1.right");var subQ8=sQuery(id+"F0.wireOp",EDGE,"E1.top");var subQ9=sQuery(id+"F0.wireOp",EDGE,"E1.left");var subQ10=sQuery(id+"F0.wireOp",EDGE,"E23.filletArc");var subQ11=sQuery(id+"F0.wireOp",EDGE,"E24.filletArc");Q0=makeQuery(id+"F2.boolean.opBoolean","SPLIT",FACE,{"disambiguationData":[TD([makeQuery(id+"F1.opExtrude","SWEPT_FACE",FACE,{"disambiguationData":[OSD([subQ6])]})])],"derivedFrom":makeQuery(id+"F1.opExtrude","CAP_FACE",FACE,{"disambiguationData":[OSD([subQ6,subQ8,subQ9,subQ7,subQ4,subQ3,subQ2,subQ1,subQ0,subQ5,subQ10,subQ11])],"isStart":true})});}
            var sketch = newSketch(context, id + "F16", { "sketchPlane" : qUnion([Q0])});
            skLineSegment(sketch, "E79", {"start": v(0, 90) * mm, "end": v(0, 146.76) * mm, "construction": true});
            skCircle(sketch, "E80", {"center": v(0, 120) * mm, "radius": 6 * mm});
            skLineSegment(sketch, "E81", {"start": v(-33, 90) * mm, "end": v(-15, 108) * mm});
            skLineSegment(sketch, "E82", {"start": v(-15, 108) * mm, "end": v(-15, 120) * mm});
            skLineSegment(sketch, "E83", {"start": v(33, 90) * mm, "end": v(15, 108) * mm});
            skLineSegment(sketch, "E84", {"start": v(15, 108) * mm, "end": v(15, 120) * mm});
            skArc(sketch, "E85", {"start": v(15, 120) * mm, "mid": v(0, 135) * mm, "end": v(-15, 120) * mm});
            skLineSegment(sketch, "E86", {"start": v(-80, 0) * mm, "end": v(80, 0) * mm, "construction": true});
            skLineSegment(sketch, "E87.MirrorCS", {"start": v(15, -108) * mm, "end": v(15, -120) * mm});
            skCircle(sketch, "E88.MirrorC", {"center": v(0, -120) * mm, "radius": 6 * mm});
            skLineSegment(sketch, "E89.MirrorCS", {"start": v(-15, -108) * mm, "end": v(-15, -120) * mm});
            skArc(sketch, "E90.MirrorCS", {"start": v(15, -120) * mm, "mid": v(0, -135) * mm, "end": v(-15, -120) * mm});
            skLineSegment(sketch, "E91.MirrorCS", {"start": v(33, -90) * mm, "end": v(15, -108) * mm});
            skLineSegment(sketch, "E92.MirrorCS", {"start": v(-33, -90) * mm, "end": v(-15, -108) * mm});
            skSolve(sketch);
        }
        {
            var Q0;
            Q0=makeQuery(id+"F16.imprint","IMPRINT",FACE,{"disambiguationData":[TD([[makeQuery(id+"F16.imprint","IMPRINT",EDGE,{"derivedFrom":sQuery(id+"F16.wireOp",EDGE,"E88.MirrorC")}),1.0]])]});
            var Q1;
            Q1=makeQuery(id+"F16.imprint","IMPRINT",FACE,{"disambiguationData":[TD([[makeQuery(id+"F16.imprint","IMPRINT",EDGE,{"derivedFrom":sQuery(id+"F16.wireOp",EDGE,"E80")}),-1.0]])]});
            var Q2;
            Q2=makeQuery(id+"F16.imprint","IMPRINT",FACE,{"disambiguationData":[TD([[makeQuery(id+"F16.imprint","IMPRINT",EDGE,{"derivedFrom":makeQuery(id+"F1.opExtrude","CAP_EDGE",EDGE,{"disambiguationData":[OSD([sQuery(id+"F0.wireOp",EDGE,"E1.left")])],"isStart":true})}),-1.0]])]});
            var Q3;
            Q3=makeQuery(id+"F2.opExtrude","CAP_FACE",FACE,{"disambiguationData":[OSD([sQuery(id+"F0.wireOp",EDGE,"E12"),sQuery(id+"F0.wireOp",EDGE,"E13"),sQuery(id+"F0.wireOp",EDGE,"E14"),sQuery(id+"F0.wireOp",EDGE,"E15"),sQuery(id+"F0.wireOp",EDGE,"E17.filletArc"),sQuery(id+"F0.wireOp",EDGE,"E18.filletArc"),sQuery(id+"F0.wireOp",EDGE,"E19.filletArc"),sQuery(id+"F0.wireOp",EDGE,"E20.filletArc"),sQuery(id+"F0.wireOp",EDGE,"E25.0"),sQuery(id+"F0.wireOp",EDGE,"E25.1"),sQuery(id+"F0.wireOp",EDGE,"E25.2"),sQuery(id+"F0.wireOp",EDGE,"E25.3"),sQuery(id+"F0.wireOp",EDGE,"E25.4"),sQuery(id+"F0.wireOp",EDGE,"E25.5"),sQuery(id+"F0.wireOp",EDGE,"E25.6"),sQuery(id+"F0.wireOp",EDGE,"E25.7")])],"isStart":false});
            extrude(context, id + "F17", {"entities" : qUnion([Q0, Q1, Q2]), "endBound" : BoundingType.UP_TO_SURFACE, "endBoundEntityFace" : qUnion([Q3]), "depth" : 25 * mm});
        }
    });
